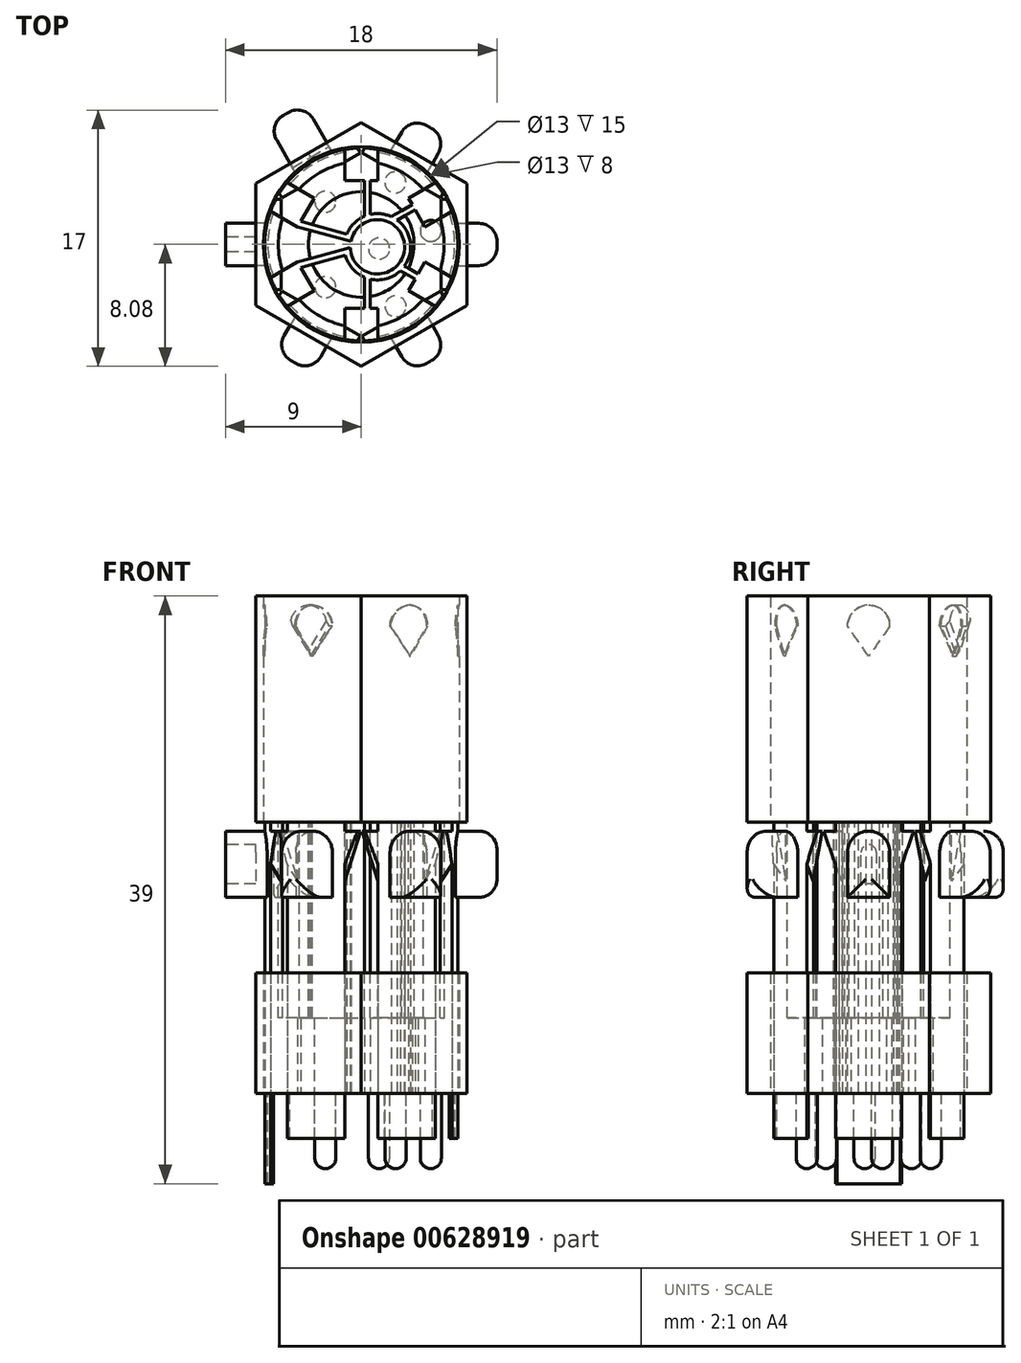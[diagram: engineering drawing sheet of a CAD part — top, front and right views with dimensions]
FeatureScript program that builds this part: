
annotation { "Feature Type Name" : "Feature", "Feature Type Description" : "" }
export const myFeature = defineFeature(function(context is Context, id is Id, definition is map)
    precondition{}
    {
        {
            var Q0;
            Q0=qCreatedBy(makeId("Top.planeOp"),FACE);
            var sketch = newSketch(context, id + "F0", { "sketchPlane" : qUnion([Q0])});
            skCircle(sketch, "E0.cCircle", {"center": v(0, 0) * mm, "radius": 7 * mm, "construction": true});
            skLineSegment(sketch, "E0.0", {"start": v(7, 4.04) * mm, "end": v(7, -4.04) * mm});
            skLineSegment(sketch, "E0.1", {"start": v(7, -4.04) * mm, "end": v(0, -8.08) * mm});
            skLineSegment(sketch, "E0.2", {"start": v(0, -8.08) * mm, "end": v(-7, -4.04) * mm});
            skLineSegment(sketch, "E0.3", {"start": v(-7, -4.04) * mm, "end": v(-7, 4.04) * mm});
            skLineSegment(sketch, "E0.4", {"start": v(-7, 4.04) * mm, "end": v(0, 8.08) * mm});
            skLineSegment(sketch, "E0.5", {"start": v(0, 8.08) * mm, "end": v(7, 4.04) * mm});
            skPoint(sketch, "E0.0.midPoint", {"position": v(7, 0) * mm});
            skCircle(sketch, "E1", {"center": v(0, 0) * mm, "radius": 6.4 * mm});
            skLineSegment(sketch, "E2", {"start": v(-1.1, 7.45) * mm, "end": v(1.1, 7.45) * mm});
            skLineSegment(sketch, "E3", {"start": v(1.1, 7.45) * mm, "end": v(1.1, 4.25) * mm});
            skLineSegment(sketch, "E4", {"start": v(1.1, -7.45) * mm, "end": v(-1.1, -7.45) * mm});
            skLineSegment(sketch, "E5", {"start": v(-1.1, -7.45) * mm, "end": v(-1.1, -4.25) * mm});
            skLineSegment(sketch, "E6", {"start": v(-7, 2.77) * mm, "end": v(-5.9, 4.68) * mm});
            skLineSegment(sketch, "E7", {"start": v(-5.9, 4.68) * mm, "end": v(-3.13, 3.08) * mm});
            skLineSegment(sketch, "E8", {"start": v(7, -2.77) * mm, "end": v(5.9, -4.68) * mm});
            skLineSegment(sketch, "E9", {"start": v(5.9, -4.68) * mm, "end": v(3.13, -3.08) * mm});
            skLineSegment(sketch, "E10", {"start": v(-7, -2.77) * mm, "end": v(-5.9, -4.68) * mm});
            skLineSegment(sketch, "E11", {"start": v(-5.9, -4.68) * mm, "end": v(-3.13, -3.08) * mm});
            skLineSegment(sketch, "E12", {"start": v(7, 2.77) * mm, "end": v(5.9, 4.68) * mm});
            skLineSegment(sketch, "E13", {"start": v(5.9, 4.68) * mm, "end": v(3.13, 3.08) * mm});
            skLineSegment(sketch, "E14", {"start": v(-1.1, 4.25) * mm, "end": v(1.1, 4.25) * mm});
            skLineSegment(sketch, "E15", {"start": v(-3.13, 3.08) * mm, "end": v(-4.23, 1.17) * mm});
            skLineSegment(sketch, "E16", {"start": v(-4.23, -1.17) * mm, "end": v(-3.13, -3.08) * mm});
            skLineSegment(sketch, "E17", {"start": v(-1.1, -4.25) * mm, "end": v(1.1, -4.25) * mm});
            skLineSegment(sketch, "E18", {"start": v(3.13, -3.08) * mm, "end": v(4.23, -1.17) * mm});
            skLineSegment(sketch, "E19", {"start": v(4.23, 1.17) * mm, "end": v(3.13, 3.08) * mm});
            skLineSegment(sketch, "E20.trimOffspring", {"start": v(4.23, 1.17) * mm, "end": v(7, 2.77) * mm});
            skLineSegment(sketch, "E21.trimOffspring", {"start": v(-4.23, -1.17) * mm, "end": v(-7, -2.77) * mm});
            skLineSegment(sketch, "E22.trimOffspring", {"start": v(-4.23, 1.17) * mm, "end": v(-7, 2.77) * mm});
            skLineSegment(sketch, "E23.trimOffspring", {"start": v(1.1, -4.25) * mm, "end": v(1.1, -7.45) * mm});
            skLineSegment(sketch, "E24.trimOffspring", {"start": v(4.23, -1.17) * mm, "end": v(7, -2.77) * mm});
            skLineSegment(sketch, "E25.trimOffspring", {"start": v(-1.1, 4.25) * mm, "end": v(-1.1, 7.45) * mm});
            skLineSegment(sketch, "E26", {"start": v(-4.02, 1.53) * mm, "end": v(-0.96, 0.68) * mm});
            skLineSegment(sketch, "E27", {"start": v(3.58, -2.3) * mm, "end": v(2.6, -1.75) * mm});
            skLineSegment(sketch, "E28", {"start": v(0.2, 4.25) * mm, "end": v(0.2, 1.86) * mm});
            skLineSegment(sketch, "E29", {"start": v(0.2, -4.25) * mm, "end": v(0.6, -4.25) * mm});
            skLineSegment(sketch, "E30", {"start": v(0.6, -4.25) * mm, "end": v(0.6, -2.3) * mm});
            skLineSegment(sketch, "E31", {"start": v(0.6, 4.25) * mm, "end": v(0.2, 4.25) * mm});
            skLineSegment(sketch, "E32", {"start": v(3.38, 2.64) * mm, "end": v(2, 1.84) * mm});
            skLineSegment(sketch, "E33", {"start": v(-4.23, -1.17) * mm, "end": v(-4.02, -1.53) * mm});
            skLineSegment(sketch, "E34", {"start": v(-4.02, -1.53) * mm, "end": v(-1.06, -0.7) * mm});
            skArc(sketch, "E35", {"start": v(2.86, -1.44) * mm, "mid": v(3.25, 0.18) * mm, "end": v(2.39, 1.6) * mm});
            skArc(sketch, "E36", {"start": v(2, 1.84) * mm, "mid": v(1.3, 2.03) * mm, "end": v(0.6, 2) * mm});
            skArc(sketch, "E37", {"start": v(0.6, -2.3) * mm, "mid": v(1.67, -2.28) * mm, "end": v(2.6, -1.75) * mm});
            skArc(sketch, "E38", {"start": v(-1.06, -0.7) * mm, "mid": v(-0.6, -1.59) * mm, "end": v(0.2, -2.18) * mm});
            skArc(sketch, "E39", {"start": v(0.2, 1.86) * mm, "mid": v(-0.5, 1.38) * mm, "end": v(-0.96, 0.68) * mm});
            skLineSegment(sketch, "E40.trimOffspring", {"start": v(0.2, -2.18) * mm, "end": v(0.2, -4.25) * mm});
            skLineSegment(sketch, "E41.trimOffspring", {"start": v(-0.7, 0.2) * mm, "end": v(-4.23, 1.17) * mm});
            skLineSegment(sketch, "E42.trimOffspring", {"start": v(2.86, -1.44) * mm, "end": v(3.78, -1.94) * mm});
            skLineSegment(sketch, "E43.trimOffspring", {"start": v(2.39, 1.6) * mm, "end": v(3.58, 2.3) * mm});
            skLineSegment(sketch, "E44.trimOffspring", {"start": v(-0.73, -0.2) * mm, "end": v(-4.23, -1.17) * mm});
            skLineSegment(sketch, "E45.trimOffspring", {"start": v(0.6, 2) * mm, "end": v(0.6, 4.25) * mm});
            skArc(sketch, "E46", {"start": v(-0.73, -0.2) * mm, "mid": v(2.87, -0.31) * mm, "end": v(-0.7, 0.2) * mm});
            skSolve(sketch);
        }
        {
            var Q0;
            {var subQ3=sQuery(id+"F0.wireOp",EDGE,"E1");var subQ5=sQuery(id+"F0.wireOp",EDGE,"E22.trimOffspring");var subQ12=makeQuery(id+"F0.imprint","INTERSECT",VERTEX,{"derivedFrom":[subQ3,subQ5]});Q0=makeQuery(id+"F0.imprint","IMPRINT",FACE,{"disambiguationData":[TD([[makeQuery(id+"F0.imprint","IMPRINT",EDGE,{"disambiguationData":[TD([[subQ12,-1.0]])],"derivedFrom":subQ3}),1.0]])]});}
            var Q1;
            {var subQ5=sQuery(id+"F0.wireOp",EDGE,"E25.trimOffspring");var subQ10=sQuery(id+"F0.wireOp",EDGE,"E1");var subQ12=makeQuery(id+"F0.imprint","INTERSECT",VERTEX,{"derivedFrom":[subQ10,subQ5]});Q1=makeQuery(id+"F0.imprint","IMPRINT",FACE,{"disambiguationData":[TD([[makeQuery(id+"F0.imprint","IMPRINT",EDGE,{"disambiguationData":[TD([[subQ12,-1.0]])],"derivedFrom":subQ10}),1.0]])]});}
            var Q2;
            {var subQ1=sQuery(id+"F0.wireOp",EDGE,"E13");var subQ3=sQuery(id+"F0.wireOp",EDGE,"E1");var subQ4=makeQuery(id+"F0.imprint","INTERSECT",VERTEX,{"derivedFrom":[subQ3,subQ1]});Q2=makeQuery(id+"F0.imprint","IMPRINT",FACE,{"disambiguationData":[TD([[makeQuery(id+"F0.imprint","IMPRINT",EDGE,{"disambiguationData":[TD([[subQ4,-1.0]])],"derivedFrom":subQ3}),1.0]])]});}
            var Q3;
            {var subQ0=sQuery(id+"F0.wireOp",EDGE,"E20.trimOffspring");var subQ3=sQuery(id+"F0.wireOp",EDGE,"E1");var subQ4=makeQuery(id+"F0.imprint","INTERSECT",VERTEX,{"derivedFrom":[subQ3,subQ0]});Q3=makeQuery(id+"F0.imprint","IMPRINT",FACE,{"disambiguationData":[TD([[makeQuery(id+"F0.imprint","IMPRINT",EDGE,{"disambiguationData":[TD([[subQ4,1.0]])],"derivedFrom":subQ3}),1.0]])]});}
            var Q4;
            {var subQ0=sQuery(id+"F0.wireOp",EDGE,"E23.trimOffspring");var subQ8=sQuery(id+"F0.wireOp",EDGE,"E1");var subQ12=makeQuery(id+"F0.imprint","INTERSECT",VERTEX,{"derivedFrom":[subQ8,subQ0]});Q4=makeQuery(id+"F0.imprint","IMPRINT",FACE,{"disambiguationData":[TD([[makeQuery(id+"F0.imprint","IMPRINT",EDGE,{"disambiguationData":[TD([[subQ12,-1.0]])],"derivedFrom":subQ8}),1.0]])]});}
            var Q5;
            {var subQ1=sQuery(id+"F0.wireOp",EDGE,"E11");var subQ5=sQuery(id+"F0.wireOp",EDGE,"E1");var subQ6=makeQuery(id+"F0.imprint","INTERSECT",VERTEX,{"derivedFrom":[subQ5,subQ1]});Q5=makeQuery(id+"F0.imprint","IMPRINT",FACE,{"disambiguationData":[TD([[makeQuery(id+"F0.imprint","IMPRINT",EDGE,{"disambiguationData":[TD([[subQ6,-1.0]])],"derivedFrom":subQ5}),1.0]])]});}
            extrude(context, id + "F1", {"entities" : qUnion([Q0, Q1, Q2, Q3, Q4, Q5]), "depth" : 33 * mm, "offsetDistance" : 25 * mm});
        }
        {
            var Q0;
            Q0=makeQuery(id+"F1.opExtrude","CAP_FACE",FACE,{"disambiguationData":[OSD([sQuery(id+"F0.wireOp",EDGE,"E1"),sQuery(id+"F0.wireOp",EDGE,"E7"),sQuery(id+"F0.wireOp",EDGE,"E14"),sQuery(id+"F0.wireOp",EDGE,"E15"),sQuery(id+"F0.wireOp",EDGE,"E25.trimOffspring"),sQuery(id+"F0.wireOp",EDGE,"E26"),sQuery(id+"F0.wireOp",EDGE,"E28")])],"isStart":false});
            cPlane(context, id + "F2", {"entities" : qUnion([Q0]), "cplaneType" : CPlaneType.OFFSET, "offset" : 0 * mm, "width" : 150 * mm, "height" : 150 * mm});
        }
        {
            var Q0;
            Q0=qCreatedBy(id+"F2.planeOp",FACE);
            var sketch = newSketch(context, id + "F3", { "sketchPlane" : qUnion([Q0])});
            skCircle(sketch, "E47", {"center": v(0, 0) * mm, "radius": 3.5 * mm});
            skCircle(sketch, "E48", {"center": v(0, 0) * mm, "radius": 5.5 * mm});
            skSolve(sketch);
        }
        {
            var Q0;
            Q0=makeQuery(id+"F3.imprint","IMPRINT",FACE,{"disambiguationData":[TD([[makeQuery(id+"F3.imprint","IMPRINT",EDGE,{"derivedFrom":sQuery(id+"F3.wireOp",EDGE,"E47")}),-1.0]])]});
            extrude(context, id + "F4", {"entities" : qUnion([Q0]), "operationType" : NewBodyOperationType.REMOVE, "oppositeDirection" : true, "depth" : 28 * mm, "offsetDistance" : 25 * mm});
        }
        {
            var Q0;
            Q0=makeQuery(id+"F1.opExtrude","CAP_FACE",FACE,{"disambiguationData":[OSD([sQuery(id+"F0.wireOp",EDGE,"E1"),sQuery(id+"F0.wireOp",EDGE,"E3"),sQuery(id+"F0.wireOp",EDGE,"E13"),sQuery(id+"F0.wireOp",EDGE,"E14"),sQuery(id+"F0.wireOp",EDGE,"E19"),sQuery(id+"F0.wireOp",EDGE,"E30"),sQuery(id+"F0.wireOp",EDGE,"E32")])],"isStart":true});
            var sketch = newSketch(context, id + "F5", { "sketchPlane" : qUnion([Q0])});
            skCircle(sketch, "E49", {"center": v(2.26, -4.12) * mm, "radius": 0.7 * mm});
            skLineSegment(sketch, "E50.0.0", {"start": v(3.38, -2.64) * mm, "end": v(2, -1.84) * mm, "construction": true});
            skLineSegment(sketch, "E50.0.3", {"start": v(1.1, -4.25) * mm, "end": v(1.1, -6.3) * mm, "construction": true});
            skArc(sketch, "E50.0.4", {"start": v(1.1, -6.3) * mm, "mid": v(3.2, -5.54) * mm, "end": v(4.91, -4.1) * mm, "construction": true});
            skLineSegment(sketch, "E50.0.5", {"start": v(4.91, -4.1) * mm, "end": v(3.13, -3.08) * mm, "construction": true});
            skLineSegment(sketch, "E50.0.6", {"start": v(3.13, -3.08) * mm, "end": v(3.38, -2.64) * mm, "construction": true});
            skLineSegment(sketch, "E51", {"start": v(0, 0) * mm, "end": v(3.56, -6.48) * mm, "construction": true});
            skSolve(sketch);
        }
        {
            var Q0;
            Q0=qSketchRegion(id+"F5",true);
            extrude(context, id + "F6", {"entities" : qUnion([Q0]), "operationType" : NewBodyOperationType.ADD, "depth" : 5 * mm, "offsetDistance" : 25 * mm});
        }
        {
            var Q0;
            Q0=makeQuery(id+"F6.opExtrude","CAP_FACE",FACE,{"disambiguationData":[OSD([sQuery(id+"F5.wireOp",EDGE,"E49")])],"isStart":false});
            fillet(context, id + "F7", {"entities" : qUnion([Q0]), "radius" : 0.7 * mm, "tangentPropagation" : true, "allowEdgeOverflow" : false});
        }
        {
            var Q0;
            Q0=makeQuery(id+"F1.opExtrude","CAP_FACE",FACE,{"disambiguationData":[OSD([sQuery(id+"F0.wireOp",EDGE,"E1"),sQuery(id+"F0.wireOp",EDGE,"E18"),sQuery(id+"F0.wireOp",EDGE,"E19"),sQuery(id+"F0.wireOp",EDGE,"E20.trimOffspring"),sQuery(id+"F0.wireOp",EDGE,"E24.trimOffspring"),sQuery(id+"F0.wireOp",EDGE,"E26"),sQuery(id+"F0.wireOp",EDGE,"E30"),sQuery(id+"F0.wireOp",EDGE,"E34")])],"isStart":true});
            var sketch = newSketch(context, id + "F8", { "sketchPlane" : qUnion([Q0])});
            skCircle(sketch, "E52", {"center": v(4.61, -0.9) * mm, "radius": 0.7 * mm});
            skLineSegment(sketch, "E53", {"start": v(0, 0) * mm, "end": v(6.9, -1.34) * mm, "construction": true});
            skSolve(sketch);
        }
        {
            var Q0;
            Q0=makeQuery(id+"F8.imprint","IMPRINT",FACE,{"disambiguationData":[TD([[makeQuery(id+"F8.imprint","IMPRINT",EDGE,{"derivedFrom":sQuery(id+"F8.wireOp",EDGE,"E52")}),1.0]])]});
            extrude(context, id + "F9", {"entities" : qUnion([Q0]), "operationType" : NewBodyOperationType.ADD, "depth" : 5 * mm, "offsetDistance" : 25 * mm});
        }
        {
            var Q0;
            Q0=makeQuery(id+"F9.opExtrude","CAP_FACE",FACE,{"disambiguationData":[OSD([sQuery(id+"F8.wireOp",EDGE,"E52")])],"isStart":false});
            fillet(context, id + "F10", {"entities" : qUnion([Q0]), "radius" : 0.7 * mm, "tangentPropagation" : true, "allowEdgeOverflow" : false});
        }
        {
            var Q0;
            Q0=makeQuery(id+"F1.opExtrude","CAP_FACE",FACE,{"disambiguationData":[OSD([sQuery(id+"F0.wireOp",EDGE,"E1"),sQuery(id+"F0.wireOp",EDGE,"E9"),sQuery(id+"F0.wireOp",EDGE,"E17"),sQuery(id+"F0.wireOp",EDGE,"E18"),sQuery(id+"F0.wireOp",EDGE,"E23.trimOffspring"),sQuery(id+"F0.wireOp",EDGE,"E27"),sQuery(id+"F0.wireOp",EDGE,"E30")])],"isStart":true});
            var sketch = newSketch(context, id + "F11", { "sketchPlane" : qUnion([Q0])});
            skCircle(sketch, "E54", {"center": v(2.28, 4.11) * mm, "radius": 0.7 * mm});
            skLineSegment(sketch, "E55", {"start": v(0, 0) * mm, "end": v(3.87, 6.99) * mm, "construction": true});
            skSolve(sketch);
        }
        {
            var Q0;
            Q0=qSketchRegion(id+"F11",true);
            extrude(context, id + "F12", {"entities" : qUnion([Q0]), "operationType" : NewBodyOperationType.ADD, "depth" : 5 * mm, "offsetDistance" : 25 * mm});
        }
        {
            var Q0;
            Q0=makeQuery(id+"F12.opExtrude","CAP_FACE",FACE,{"disambiguationData":[OSD([sQuery(id+"F11.wireOp",EDGE,"E54")])],"isStart":false});
            fillet(context, id + "F13", {"entities" : qUnion([Q0]), "radius" : 0.7 * mm, "tangentPropagation" : true, "allowEdgeOverflow" : false});
        }
        {
            var Q0;
            Q0=makeQuery(id+"F1.opExtrude","CAP_FACE",FACE,{"disambiguationData":[OSD([sQuery(id+"F0.wireOp",EDGE,"E1"),sQuery(id+"F0.wireOp",EDGE,"E5"),sQuery(id+"F0.wireOp",EDGE,"E11"),sQuery(id+"F0.wireOp",EDGE,"E16"),sQuery(id+"F0.wireOp",EDGE,"E17"),sQuery(id+"F0.wireOp",EDGE,"E27"),sQuery(id+"F0.wireOp",EDGE,"E28"),sQuery(id+"F0.wireOp",EDGE,"E34")])],"isStart":true});
            var sketch = newSketch(context, id + "F14", { "sketchPlane" : qUnion([Q0])});
            skLineSegment(sketch, "E56", {"start": v(0, 0) * mm, "end": v(-6.07, 7.24) * mm, "construction": true});
            skCircle(sketch, "E57", {"center": v(-2.38, 2.83) * mm, "radius": 0.7 * mm});
            skSolve(sketch);
        }
        {
            var Q0;
            Q0=makeQuery(id+"F14.imprint","IMPRINT",FACE,{"disambiguationData":[TD([[makeQuery(id+"F14.imprint","IMPRINT",EDGE,{"derivedFrom":sQuery(id+"F14.wireOp",EDGE,"E57")}),1.0]])]});
            extrude(context, id + "F15", {"entities" : qUnion([Q0]), "operationType" : NewBodyOperationType.ADD, "depth" : 5 * mm, "offsetDistance" : 25 * mm});
        }
        {
            var Q0;
            Q0=makeQuery(id+"F15.opExtrude","CAP_FACE",FACE,{"disambiguationData":[OSD([sQuery(id+"F14.wireOp",EDGE,"E57")])],"isStart":false});
            fillet(context, id + "F16", {"entities" : qUnion([Q0]), "radius" : 0.7 * mm, "tangentPropagation" : true, "allowEdgeOverflow" : false});
        }
        {
            var Q0;
            Q0=makeQuery(id+"F1.opExtrude","CAP_FACE",FACE,{"disambiguationData":[OSD([sQuery(id+"F0.wireOp",EDGE,"E1"),sQuery(id+"F0.wireOp",EDGE,"E7"),sQuery(id+"F0.wireOp",EDGE,"E14"),sQuery(id+"F0.wireOp",EDGE,"E15"),sQuery(id+"F0.wireOp",EDGE,"E25.trimOffspring"),sQuery(id+"F0.wireOp",EDGE,"E26"),sQuery(id+"F0.wireOp",EDGE,"E28"),sQuery(id+"F0.wireOp",EDGE,"E39")])],"isStart":true});
            var sketch = newSketch(context, id + "F17", { "sketchPlane" : qUnion([Q0])});
            skLineSegment(sketch, "E58", {"start": v(0, 0) * mm, "end": v(-5.7, -6.78) * mm, "construction": true});
            skCircle(sketch, "E59", {"center": v(-2.38, -2.83) * mm, "radius": 0.7 * mm});
            skSolve(sketch);
        }
        {
            var Q0;
            Q0=makeQuery(id+"F17.imprint","IMPRINT",FACE,{"disambiguationData":[TD([[makeQuery(id+"F17.imprint","IMPRINT",EDGE,{"derivedFrom":sQuery(id+"F17.wireOp",EDGE,"E59")}),1.0]])]});
            extrude(context, id + "F18", {"entities" : qUnion([Q0]), "operationType" : NewBodyOperationType.ADD, "depth" : 5 * mm, "offsetDistance" : 25 * mm});
        }
        {
            var Q0;
            Q0=makeQuery(id+"F18.opExtrude","CAP_FACE",FACE,{"disambiguationData":[OSD([sQuery(id+"F17.wireOp",EDGE,"E59")])],"isStart":false});
            fillet(context, id + "F19", {"entities" : qUnion([Q0]), "radius" : 0.7 * mm, "tangentPropagation" : true, "allowEdgeOverflow" : false});
        }
        {
            var Q0;
            Q0=makeQuery(id+"F1.opExtrude","CAP_FACE",FACE,{"disambiguationData":[OSD([sQuery(id+"F0.wireOp",EDGE,"E1"),sQuery(id+"F0.wireOp",EDGE,"E21.trimOffspring"),sQuery(id+"F0.wireOp",EDGE,"E22.trimOffspring"),sQuery(id+"F0.wireOp",EDGE,"E41.trimOffspring"),sQuery(id+"F0.wireOp",EDGE,"E44.trimOffspring"),sQuery(id+"F0.wireOp",EDGE,"E46")])],"isStart":true});
            var sketch = newSketch(context, id + "F20", { "sketchPlane" : qUnion([Q0])});
            skLineSegment(sketch, "E60", {"start": v(0, 0) * mm, "end": v(8.48, 1.96) * mm, "construction": true});
            skCircle(sketch, "E61", {"center": v(1.18, 0.27) * mm, "radius": 0.7 * mm});
            skSolve(sketch);
        }
        {
            var Q0;
            Q0=makeQuery(id+"F20.imprint","IMPRINT",FACE,{"disambiguationData":[TD([[makeQuery(id+"F20.imprint","IMPRINT",EDGE,{"derivedFrom":sQuery(id+"F20.wireOp",EDGE,"E61")}),1.0]])]});
            extrude(context, id + "F21", {"entities" : qUnion([Q0]), "operationType" : NewBodyOperationType.ADD, "depth" : 5 * mm, "offsetDistance" : 25 * mm});
        }
        {
            var Q0;
            Q0=makeQuery(id+"F21.opExtrude","CAP_FACE",FACE,{"disambiguationData":[OSD([sQuery(id+"F20.wireOp",EDGE,"E61")])],"isStart":false});
            fillet(context, id + "F22", {"entities" : qUnion([Q0]), "radius" : 0.7 * mm, "tangentPropagation" : true, "allowEdgeOverflow" : false});
        }
        {
            var Q0;
            {var subQ0=sQuery(id+"F0.wireOp",EDGE,"E41.trimOffspring");var subQ1=sQuery(id+"F0.wireOp",EDGE,"E46");var subQ2=sQuery(id+"F0.wireOp",EDGE,"E44.trimOffspring");Q0=makeQuery(id+"F4.boolean.opBoolean","SPLIT",FACE,{"disambiguationData":[TD([makeQuery(id+"F1.opExtrude","SWEPT_FACE",FACE,{"disambiguationData":[OSD([subQ0])]})])],"derivedFrom":makeQuery(id+"F1.opExtrude","CAP_FACE",FACE,{"disambiguationData":[OSD([sQuery(id+"F0.wireOp",EDGE,"E1"),sQuery(id+"F0.wireOp",EDGE,"E21.trimOffspring"),sQuery(id+"F0.wireOp",EDGE,"E22.trimOffspring"),subQ0,subQ2,subQ1])],"isStart":false})});}
            cPlane(context, id + "F23", {"entities" : qUnion([Q0]), "cplaneType" : CPlaneType.OFFSET, "offset" : 0 * mm, "width" : 150 * mm, "height" : 150 * mm});
        }
        {
            var Q0;
            Q0=qCreatedBy(id+"F23.planeOp",FACE);
            var sketch = newSketch(context, id + "F24", { "sketchPlane" : qUnion([Q0])});
            skCircle(sketch, "E62", {"center": v(0, 0) * mm, "radius": 7 * mm});
            skSolve(sketch);
        }
        {
            var Q0;
            Q0=makeQuery(id+"F24.imprint","IMPRINT",FACE,{"disambiguationData":[TD([[makeQuery(id+"F24.imprint","IMPRINT",EDGE,{"derivedFrom":sQuery(id+"F24.wireOp",EDGE,"E62")}),1.0]])]});
            extrude(context, id + "F25", {"entities" : qUnion([Q0]), "operationType" : NewBodyOperationType.REMOVE, "oppositeDirection" : true, "depth" : 15 * mm, "offsetDistance" : 25 * mm});
        }
        {
            var Q0;
            Q0=makeQuery(id+"F1.opExtrude","CAP_FACE",FACE,{"disambiguationData":[OSD([sQuery(id+"F0.wireOp",EDGE,"E1"),sQuery(id+"F0.wireOp",EDGE,"E18"),sQuery(id+"F0.wireOp",EDGE,"E19"),sQuery(id+"F0.wireOp",EDGE,"E20.trimOffspring"),sQuery(id+"F0.wireOp",EDGE,"E24.trimOffspring"),sQuery(id+"F0.wireOp",EDGE,"E35"),sQuery(id+"F0.wireOp",EDGE,"E42.trimOffspring"),sQuery(id+"F0.wireOp",EDGE,"E43.trimOffspring")])],"isStart":true});
            var sketch = newSketch(context, id + "F26", { "sketchPlane" : qUnion([Q0])});
            skArc(sketch, "E63.0", {"start": v(6.01, 2.2) * mm, "mid": v(6.4, 0) * mm, "end": v(6.01, -2.2) * mm});
            skArc(sketch, "E64.0", {"start": v(5.82, 2.13) * mm, "mid": v(6.2, 0) * mm, "end": v(5.82, -2.13) * mm});
            skLineSegment(sketch, "E65.0", {"start": v(4.88, -1.55) * mm, "end": v(6.01, -2.2) * mm});
            skLineSegment(sketch, "E66.0", {"start": v(4.23, 1.17) * mm, "end": v(6.01, 2.2) * mm});
            skSolve(sketch);
        }
        {
            var Q0;
            {var subQ0=sQuery(id+"F26.wireOp",EDGE,"E63.0");Q0=makeQuery(id+"F26.imprint","IMPRINT",FACE,{"disambiguationData":[TD([[makeQuery(id+"F26.imprint","IMPRINT",EDGE,{"derivedFrom":subQ0}),-1.0]])]});}
            extrude(context, id + "F27", {"entities" : qUnion([Q0]), "operationType" : NewBodyOperationType.ADD, "depth" : 3 * mm, "offsetDistance" : 25 * mm});
        }
        {
            var Q0;
            Q0=makeQuery(id+"F1.opExtrude","CAP_FACE",FACE,{"disambiguationData":[OSD([sQuery(id+"F0.wireOp",EDGE,"E1"),sQuery(id+"F0.wireOp",EDGE,"E9"),sQuery(id+"F0.wireOp",EDGE,"E17"),sQuery(id+"F0.wireOp",EDGE,"E18"),sQuery(id+"F0.wireOp",EDGE,"E23.trimOffspring"),sQuery(id+"F0.wireOp",EDGE,"E27"),sQuery(id+"F0.wireOp",EDGE,"E30"),sQuery(id+"F0.wireOp",EDGE,"E37")])],"isStart":true});
            var sketch = newSketch(context, id + "F28", { "sketchPlane" : qUnion([Q0])});
            skArc(sketch, "E67.0", {"start": v(1.1, 6.3) * mm, "mid": v(3.2, 5.54) * mm, "end": v(4.91, 4.1) * mm});
            skLineSegment(sketch, "E68.0", {"start": v(1.1, 4.25) * mm, "end": v(1.1, 6.3) * mm});
            skLineSegment(sketch, "E69.0", {"start": v(4.91, 4.1) * mm, "end": v(3.13, 3.08) * mm});
            skArc(sketch, "E70.0", {"start": v(1.07, 6.1) * mm, "mid": v(3.1, 5.37) * mm, "end": v(4.76, 3.98) * mm});
            skSolve(sketch);
        }
        {
            var Q0;
            Q0=qSketchRegion(id+"F28",true);
            extrude(context, id + "F29", {"entities" : qUnion([Q0]), "operationType" : NewBodyOperationType.ADD, "depth" : 3 * mm, "offsetDistance" : 25 * mm});
        }
        {
            var Q0;
            Q0=makeQuery(id+"F1.opExtrude","CAP_FACE",FACE,{"disambiguationData":[OSD([sQuery(id+"F0.wireOp",EDGE,"E1"),sQuery(id+"F0.wireOp",EDGE,"E5"),sQuery(id+"F0.wireOp",EDGE,"E11"),sQuery(id+"F0.wireOp",EDGE,"E16"),sQuery(id+"F0.wireOp",EDGE,"E17"),sQuery(id+"F0.wireOp",EDGE,"E34"),sQuery(id+"F0.wireOp",EDGE,"E38"),sQuery(id+"F0.wireOp",EDGE,"E40.trimOffspring")])],"isStart":true});
            var sketch = newSketch(context, id + "F30", { "sketchPlane" : qUnion([Q0])});
            skArc(sketch, "E71.0", {"start": v(-4.91, 4.1) * mm, "mid": v(-3.2, 5.54) * mm, "end": v(-1.1, 6.3) * mm});
            skLineSegment(sketch, "E72.0", {"start": v(-1.1, 6.3) * mm, "end": v(-1.1, 4.25) * mm});
            skLineSegment(sketch, "E73.0", {"start": v(-4.91, 4.1) * mm, "end": v(-3.13, 3.08) * mm});
            skArc(sketch, "E74.0", {"start": v(-4.76, 3.98) * mm, "mid": v(-3.1, 5.37) * mm, "end": v(-1.07, 6.1) * mm});
            skSolve(sketch);
        }
        {
            var Q0;
            Q0=qSketchRegion(id+"F30",true);
            extrude(context, id + "F31", {"entities" : qUnion([Q0]), "operationType" : NewBodyOperationType.ADD, "depth" : 3 * mm, "offsetDistance" : 25 * mm});
        }
        {
            var Q0;
            Q0=makeQuery(id+"F1.opExtrude","CAP_FACE",FACE,{"disambiguationData":[OSD([sQuery(id+"F0.wireOp",EDGE,"E1"),sQuery(id+"F0.wireOp",EDGE,"E21.trimOffspring"),sQuery(id+"F0.wireOp",EDGE,"E22.trimOffspring"),sQuery(id+"F0.wireOp",EDGE,"E41.trimOffspring"),sQuery(id+"F0.wireOp",EDGE,"E44.trimOffspring"),sQuery(id+"F0.wireOp",EDGE,"E46")])],"isStart":true});
            var sketch = newSketch(context, id + "F32", { "sketchPlane" : qUnion([Q0])});
            skLineSegment(sketch, "E75.0", {"start": v(-4.23, 1.17) * mm, "end": v(-6.01, 2.2) * mm});
            skArc(sketch, "E76.0", {"start": v(-6.01, -2.2) * mm, "mid": v(-6.4, 0) * mm, "end": v(-6.01, 2.2) * mm});
            skLineSegment(sketch, "E77.0", {"start": v(-4.23, -1.17) * mm, "end": v(-6.01, -2.2) * mm});
            skArc(sketch, "E78.0", {"start": v(-5.82, -2.13) * mm, "mid": v(-6.2, 0) * mm, "end": v(-5.82, 2.13) * mm});
            skSolve(sketch);
        }
        {
            var Q0;
            Q0=qSketchRegion(id+"F32",true);
            extrude(context, id + "F33", {"entities" : qUnion([Q0]), "operationType" : NewBodyOperationType.ADD, "depth" : 6 * mm, "offsetDistance" : 25 * mm});
        }
        {
            var Q0;
            Q0=makeQuery(id+"F1.opExtrude","CAP_FACE",FACE,{"disambiguationData":[OSD([sQuery(id+"F0.wireOp",EDGE,"E1"),sQuery(id+"F0.wireOp",EDGE,"E7"),sQuery(id+"F0.wireOp",EDGE,"E14"),sQuery(id+"F0.wireOp",EDGE,"E15"),sQuery(id+"F0.wireOp",EDGE,"E25.trimOffspring"),sQuery(id+"F0.wireOp",EDGE,"E26"),sQuery(id+"F0.wireOp",EDGE,"E28"),sQuery(id+"F0.wireOp",EDGE,"E39")])],"isStart":true});
            var sketch = newSketch(context, id + "F34", { "sketchPlane" : qUnion([Q0])});
            skArc(sketch, "E79.0", {"start": v(-1.1, -6.3) * mm, "mid": v(-3.2, -5.54) * mm, "end": v(-4.91, -4.1) * mm});
            skLineSegment(sketch, "E80.0", {"start": v(-1.1, -4.25) * mm, "end": v(-1.1, -6.3) * mm});
            skLineSegment(sketch, "E81.0", {"start": v(-4.91, -4.1) * mm, "end": v(-3.13, -3.08) * mm});
            skArc(sketch, "E82.0", {"start": v(-1.07, -6.1) * mm, "mid": v(-3.1, -5.37) * mm, "end": v(-4.76, -3.98) * mm});
            skSolve(sketch);
        }
        {
            var Q0;
            Q0=qSketchRegion(id+"F34",true);
            extrude(context, id + "F35", {"entities" : qUnion([Q0]), "operationType" : NewBodyOperationType.ADD, "depth" : 3 * mm, "offsetDistance" : 25 * mm});
        }
        {
            var Q0;
            Q0=makeQuery(id+"F1.opExtrude","CAP_FACE",FACE,{"disambiguationData":[OSD([sQuery(id+"F0.wireOp",EDGE,"E1"),sQuery(id+"F0.wireOp",EDGE,"E3"),sQuery(id+"F0.wireOp",EDGE,"E13"),sQuery(id+"F0.wireOp",EDGE,"E14"),sQuery(id+"F0.wireOp",EDGE,"E19"),sQuery(id+"F0.wireOp",EDGE,"E32"),sQuery(id+"F0.wireOp",EDGE,"E36"),sQuery(id+"F0.wireOp",EDGE,"E45.trimOffspring")])],"isStart":true});
            var sketch = newSketch(context, id + "F36", { "sketchPlane" : qUnion([Q0])});
            skArc(sketch, "E83.0", {"start": v(4.91, -4.1) * mm, "mid": v(3.2, -5.54) * mm, "end": v(1.1, -6.3) * mm});
            skLineSegment(sketch, "E84.0", {"start": v(1.1, -6.3) * mm, "end": v(1.1, -4.25) * mm});
            skLineSegment(sketch, "E85.0", {"start": v(4.91, -4.1) * mm, "end": v(3.13, -3.08) * mm});
            skArc(sketch, "E86.0", {"start": v(4.76, -3.98) * mm, "mid": v(3.1, -5.37) * mm, "end": v(1.07, -6.1) * mm});
            skSolve(sketch);
        }
        {
            var Q0;
            Q0=qSketchRegion(id+"F36",true);
            extrude(context, id + "F37", {"entities" : qUnion([Q0]), "operationType" : NewBodyOperationType.ADD, "depth" : 3 * mm, "offsetDistance" : 25 * mm});
        }
        {
            var Q0;
            Q0=qCreatedBy(makeId("Top.planeOp"),FACE);
            var sketch = newSketch(context, id + "F38", { "sketchPlane" : qUnion([Q0])});
            skCircle(sketch, "E87.cCircle", {"center": v(0, 0) * mm, "radius": 7 * mm, "construction": true});
            skLineSegment(sketch, "E87.0", {"start": v(7, 4.04) * mm, "end": v(7, -4.04) * mm});
            skLineSegment(sketch, "E87.1", {"start": v(7, -4.04) * mm, "end": v(0, -8.08) * mm});
            skLineSegment(sketch, "E87.2", {"start": v(0, -8.08) * mm, "end": v(-7, -4.04) * mm});
            skLineSegment(sketch, "E87.3", {"start": v(-7, -4.04) * mm, "end": v(-7, 4.04) * mm});
            skLineSegment(sketch, "E87.4", {"start": v(-7, 4.04) * mm, "end": v(0, 8.08) * mm});
            skLineSegment(sketch, "E87.5", {"start": v(0, 8.08) * mm, "end": v(7, 4.04) * mm});
            skPoint(sketch, "E87.0.midPoint", {"position": v(7, 0) * mm});
            skCircle(sketch, "E88", {"center": v(0, 0) * mm, "radius": 6.5 * mm});
            skSolve(sketch);
        }
        {
            var Q0;
            Q0=makeQuery(id+"F38.imprint","IMPRINT",FACE,{"disambiguationData":[TD([[makeQuery(id+"F38.imprint","IMPRINT",EDGE,{"derivedFrom":sQuery(id+"F38.wireOp",EDGE,"E87.0")}),-1.0]])]});
            extrude(context, id + "F39", {"entities" : qUnion([Q0]), "depth" : 33 * mm, "offsetDistance" : 25 * mm});
        }
        {
            var Q0;
            Q0=makeQuery(id+"F39.opExtrude","SWEPT_FACE",FACE,{"disambiguationData":[OSD([sQuery(id+"F38.wireOp",EDGE,"E87.5")])]});
            var sketch = newSketch(context, id + "F40", { "sketchPlane" : qUnion([Q0])});
            skLineSegment(sketch, "E89", {"start": v(-4.04, 16) * mm, "end": v(4.04, 16) * mm, "construction": true});
            skLineSegment(sketch, "E90", {"start": v(-4.04, 31) * mm, "end": v(4.04, 31) * mm, "construction": true});
            skLineSegment(sketch, "E91", {"start": v(0, 33.33) * mm, "end": v(0, 2) * mm, "construction": true});
            skLineSegment(sketch, "E92", {"start": v(0, 6.15) * mm, "end": v(-4.04, 6.15) * mm, "construction": true});
            skLineSegment(sketch, "E93", {"start": v(0, 6.15) * mm, "end": v(4.04, 6.15) * mm, "construction": true});
            skArc(sketch, "E94", {"start": v(1.4, 31) * mm, "mid": v(0, 32.4) * mm, "end": v(-1.4, 31) * mm});
            skLineSegment(sketch, "E95", {"start": v(-1.4, 31) * mm, "end": v(0, 29) * mm});
            skLineSegment(sketch, "E96", {"start": v(0, 29) * mm, "end": v(1.4, 31) * mm});
            skArc(sketch, "E97", {"start": v(1.4, 16) * mm, "mid": v(0, 17.4) * mm, "end": v(-1.4, 16) * mm});
            skLineSegment(sketch, "E98", {"start": v(1.4, 16) * mm, "end": v(1.4, 13) * mm});
            skLineSegment(sketch, "E99", {"start": v(1.4, 13) * mm, "end": v(-1.4, 13) * mm});
            skLineSegment(sketch, "E100", {"start": v(-1.4, 13) * mm, "end": v(-1.4, 16) * mm});
            skLineSegment(sketch, "E101", {"start": v(0, 17.4) * mm, "end": v(-3, 17.4) * mm});
            skLineSegment(sketch, "E102", {"start": v(-3, 17.4) * mm, "end": v(-1.4, 13) * mm});
            skLineSegment(sketch, "E103", {"start": v(0, 17.4) * mm, "end": v(3, 17.4) * mm});
            skLineSegment(sketch, "E104", {"start": v(3, 17.4) * mm, "end": v(1.4, 13) * mm});
            skLineSegment(sketch, "E105", {"start": v(1.4, 16) * mm, "end": v(1.4, 17.4) * mm});
            skLineSegment(sketch, "E106", {"start": v(-1.4, 16) * mm, "end": v(-1.4, 17.4) * mm});
            skSolve(sketch);
        }
        {
            var Q0;
            Q0=makeQuery(id+"F39.opExtrude","SWEPT_FACE",FACE,{"disambiguationData":[OSD([sQuery(id+"F38.wireOp",EDGE,"E87.3")])]});
            var sketch = newSketch(context, id + "F41", { "sketchPlane" : qUnion([Q0])});
            skLineSegment(sketch, "E107", {"start": v(-4.04, 16) * mm, "end": v(4.04, 16) * mm, "construction": true});
            skLineSegment(sketch, "E108", {"start": v(-4.04, 31) * mm, "end": v(4.04, 31) * mm, "construction": true});
            skLineSegment(sketch, "E109", {"start": v(0, 32.47) * mm, "end": v(0, 1.15) * mm, "construction": true});
            skLineSegment(sketch, "E110", {"start": v(0, 5.3) * mm, "end": v(-4.04, 5.3) * mm, "construction": true});
            skLineSegment(sketch, "E111", {"start": v(0, 5.3) * mm, "end": v(4.04, 5.3) * mm, "construction": true});
            skArc(sketch, "E112", {"start": v(1.4, 31) * mm, "mid": v(0, 32.4) * mm, "end": v(-1.4, 31) * mm});
            skLineSegment(sketch, "E113", {"start": v(-1.4, 31) * mm, "end": v(0, 29) * mm});
            skLineSegment(sketch, "E114", {"start": v(0, 29) * mm, "end": v(1.4, 31) * mm});
            skArc(sketch, "E115", {"start": v(1.4, 16) * mm, "mid": v(0, 17.4) * mm, "end": v(-1.4, 16) * mm});
            skLineSegment(sketch, "E116", {"start": v(1.4, 16) * mm, "end": v(1.4, 13) * mm});
            skLineSegment(sketch, "E117", {"start": v(1.4, 13) * mm, "end": v(-1.4, 13) * mm});
            skLineSegment(sketch, "E118", {"start": v(-1.4, 13) * mm, "end": v(-1.4, 16) * mm});
            skLineSegment(sketch, "E119", {"start": v(0, 17.4) * mm, "end": v(-3, 17.4) * mm});
            skLineSegment(sketch, "E120", {"start": v(0, 17.4) * mm, "end": v(3, 17.4) * mm});
            skLineSegment(sketch, "E121", {"start": v(3, 17.4) * mm, "end": v(1.4, 13) * mm});
            skLineSegment(sketch, "E122", {"start": v(-1.4, 13) * mm, "end": v(-3, 17.4) * mm});
            skLineSegment(sketch, "E123", {"start": v(-1.4, 16) * mm, "end": v(-1.4, 17.4) * mm});
            skLineSegment(sketch, "E124", {"start": v(1.4, 16) * mm, "end": v(1.4, 17.4) * mm});
            skSolve(sketch);
        }
        {
            var Q0;
            Q0=makeQuery(id+"F39.opExtrude","SWEPT_FACE",FACE,{"disambiguationData":[OSD([sQuery(id+"F38.wireOp",EDGE,"E87.4")])]});
            var sketch = newSketch(context, id + "F42", { "sketchPlane" : qUnion([Q0])});
            skLineSegment(sketch, "E125", {"start": v(-4.04, 16) * mm, "end": v(4.04, 16) * mm, "construction": true});
            skLineSegment(sketch, "E126", {"start": v(-4.04, 31) * mm, "end": v(4.04, 31) * mm, "construction": true});
            skLineSegment(sketch, "E127", {"start": v(0, 33.88) * mm, "end": v(0, 2.56) * mm, "construction": true});
            skLineSegment(sketch, "E128", {"start": v(0, 6.7) * mm, "end": v(-4.04, 6.7) * mm, "construction": true});
            skLineSegment(sketch, "E129", {"start": v(0, 6.7) * mm, "end": v(4.04, 6.7) * mm, "construction": true});
            skArc(sketch, "E130", {"start": v(1.4, 31) * mm, "mid": v(0, 32.4) * mm, "end": v(-1.4, 31) * mm});
            skLineSegment(sketch, "E131", {"start": v(-1.4, 31) * mm, "end": v(0, 29) * mm});
            skLineSegment(sketch, "E132", {"start": v(0, 29) * mm, "end": v(1.4, 31) * mm});
            skArc(sketch, "E133", {"start": v(1.4, 16) * mm, "mid": v(0, 17.4) * mm, "end": v(-1.4, 16) * mm});
            skLineSegment(sketch, "E134", {"start": v(1.4, 16) * mm, "end": v(1.4, 13) * mm});
            skLineSegment(sketch, "E135", {"start": v(1.4, 13) * mm, "end": v(-1.4, 13) * mm});
            skLineSegment(sketch, "E136", {"start": v(-1.4, 13) * mm, "end": v(-1.4, 16) * mm});
            skLineSegment(sketch, "E137", {"start": v(0, 17.4) * mm, "end": v(-3, 17.4) * mm});
            skLineSegment(sketch, "E138", {"start": v(-3, 17.4) * mm, "end": v(-1.4, 13) * mm});
            skLineSegment(sketch, "E139", {"start": v(-1.4, 16) * mm, "end": v(-1.4, 17.4) * mm});
            skLineSegment(sketch, "E140", {"start": v(0, 17.4) * mm, "end": v(3, 17.4) * mm});
            skLineSegment(sketch, "E141", {"start": v(3, 17.4) * mm, "end": v(1.4, 13) * mm});
            skLineSegment(sketch, "E142", {"start": v(1.4, 16) * mm, "end": v(1.4, 17.4) * mm});
            skSolve(sketch);
        }
        {
            var Q0;
            Q0=makeQuery(id+"F39.opExtrude","SWEPT_FACE",FACE,{"disambiguationData":[OSD([sQuery(id+"F38.wireOp",EDGE,"E87.2")])]});
            var sketch = newSketch(context, id + "F43", { "sketchPlane" : qUnion([Q0])});
            skLineSegment(sketch, "E143", {"start": v(-4.04, 16) * mm, "end": v(4.04, 16) * mm, "construction": true});
            skLineSegment(sketch, "E144", {"start": v(-4.04, 31) * mm, "end": v(4.04, 31) * mm, "construction": true});
            skLineSegment(sketch, "E145", {"start": v(0, 32.25) * mm, "end": v(0, 0.93) * mm, "construction": true});
            skLineSegment(sketch, "E146", {"start": v(0, 5.07) * mm, "end": v(-4.04, 5.07) * mm, "construction": true});
            skLineSegment(sketch, "E147", {"start": v(0, 5.07) * mm, "end": v(4.04, 5.07) * mm, "construction": true});
            skArc(sketch, "E148", {"start": v(1.4, 31) * mm, "mid": v(0, 32.4) * mm, "end": v(-1.4, 31) * mm});
            skLineSegment(sketch, "E149", {"start": v(-1.4, 31) * mm, "end": v(0, 29) * mm});
            skLineSegment(sketch, "E150", {"start": v(0, 29) * mm, "end": v(1.4, 31) * mm});
            skArc(sketch, "E151", {"start": v(1.4, 16) * mm, "mid": v(0, 17.4) * mm, "end": v(-1.4, 16) * mm});
            skLineSegment(sketch, "E152", {"start": v(1.4, 16) * mm, "end": v(1.4, 13) * mm});
            skLineSegment(sketch, "E153", {"start": v(1.4, 13) * mm, "end": v(-1.4, 13) * mm});
            skLineSegment(sketch, "E154", {"start": v(-1.4, 13) * mm, "end": v(-1.4, 16) * mm});
            skLineSegment(sketch, "E155", {"start": v(0, 17.4) * mm, "end": v(-3, 17.4) * mm});
            skPoint(sketch, "E155.endSnap0", {"position": v(0, 17.4) * mm});
            skLineSegment(sketch, "E156", {"start": v(-3, 17.4) * mm, "end": v(-1.4, 13) * mm});
            skLineSegment(sketch, "E157", {"start": v(0, 17.4) * mm, "end": v(3, 17.4) * mm});
            skLineSegment(sketch, "E158", {"start": v(3, 17.4) * mm, "end": v(1.4, 13) * mm});
            skLineSegment(sketch, "E159", {"start": v(1.4, 16) * mm, "end": v(1.4, 17.4) * mm});
            skLineSegment(sketch, "E160", {"start": v(-1.4, 16) * mm, "end": v(-1.4, 17.4) * mm});
            skSolve(sketch);
        }
        {
            var Q0;
            Q0=makeQuery(id+"F39.opExtrude","SWEPT_FACE",FACE,{"disambiguationData":[OSD([sQuery(id+"F38.wireOp",EDGE,"E87.1")])]});
            var sketch = newSketch(context, id + "F44", { "sketchPlane" : qUnion([Q0])});
            skLineSegment(sketch, "E161", {"start": v(-4.04, 16) * mm, "end": v(4.04, 16) * mm, "construction": true});
            skLineSegment(sketch, "E162", {"start": v(-4.04, 31) * mm, "end": v(4.04, 31) * mm, "construction": true});
            skLineSegment(sketch, "E163", {"start": v(0, 35.95) * mm, "end": v(0, 4.63) * mm, "construction": true});
            skLineSegment(sketch, "E164", {"start": v(0, 8.76) * mm, "end": v(-4.04, 8.76) * mm, "construction": true});
            skLineSegment(sketch, "E165", {"start": v(0, 8.76) * mm, "end": v(4.04, 8.76) * mm, "construction": true});
            skArc(sketch, "E166", {"start": v(1.4, 31) * mm, "mid": v(0, 32.4) * mm, "end": v(-1.4, 31) * mm});
            skLineSegment(sketch, "E167", {"start": v(-1.4, 31) * mm, "end": v(0, 29) * mm});
            skLineSegment(sketch, "E168", {"start": v(0, 29) * mm, "end": v(1.4, 31) * mm});
            skArc(sketch, "E169", {"start": v(1.4, 16) * mm, "mid": v(0, 17.4) * mm, "end": v(-1.4, 16) * mm});
            skLineSegment(sketch, "E170", {"start": v(1.4, 16) * mm, "end": v(1.4, 13) * mm});
            skLineSegment(sketch, "E171", {"start": v(1.4, 13) * mm, "end": v(-1.4, 13) * mm});
            skLineSegment(sketch, "E172", {"start": v(-1.4, 13) * mm, "end": v(-1.4, 16) * mm});
            skLineSegment(sketch, "E173", {"start": v(0, 17.4) * mm, "end": v(-3, 17.4) * mm});
            skLineSegment(sketch, "E174", {"start": v(-3, 17.4) * mm, "end": v(-1.4, 13) * mm});
            skLineSegment(sketch, "E175", {"start": v(0, 17.4) * mm, "end": v(3, 17.4) * mm});
            skLineSegment(sketch, "E176", {"start": v(3, 17.4) * mm, "end": v(1.4, 13) * mm});
            skLineSegment(sketch, "E177", {"start": v(1.4, 16) * mm, "end": v(1.4, 17.4) * mm});
            skLineSegment(sketch, "E178", {"start": v(-1.4, 16) * mm, "end": v(-1.5, 17.4) * mm});
            skSolve(sketch);
        }
        {
            var Q0;
            Q0=makeQuery(id+"F39.opExtrude","SWEPT_FACE",FACE,{"disambiguationData":[OSD([sQuery(id+"F38.wireOp",EDGE,"E87.0")])]});
            var sketch = newSketch(context, id + "F45", { "sketchPlane" : qUnion([Q0])});
            skLineSegment(sketch, "E179", {"start": v(-4.04, 16) * mm, "end": v(4.04, 16) * mm, "construction": true});
            skLineSegment(sketch, "E180", {"start": v(-4.04, 31) * mm, "end": v(4.04, 31) * mm, "construction": true});
            skLineSegment(sketch, "E181", {"start": v(0, 33.37) * mm, "end": v(0, 2.05) * mm, "construction": true});
            skLineSegment(sketch, "E182", {"start": v(0, 6.2) * mm, "end": v(-4.04, 6.2) * mm, "construction": true});
            skLineSegment(sketch, "E183", {"start": v(0, 6.2) * mm, "end": v(4.04, 6.2) * mm, "construction": true});
            skArc(sketch, "E184", {"start": v(1.4, 31) * mm, "mid": v(0, 32.4) * mm, "end": v(-1.4, 31) * mm});
            skLineSegment(sketch, "E185", {"start": v(-1.4, 31) * mm, "end": v(0, 29) * mm});
            skLineSegment(sketch, "E186", {"start": v(0, 29) * mm, "end": v(1.4, 31) * mm});
            skArc(sketch, "E187", {"start": v(1.4, 16) * mm, "mid": v(0, 17.4) * mm, "end": v(-1.4, 16) * mm});
            skLineSegment(sketch, "E188", {"start": v(1.4, 16) * mm, "end": v(1.4, 13) * mm});
            skLineSegment(sketch, "E189", {"start": v(1.4, 13) * mm, "end": v(-1.4, 13) * mm});
            skLineSegment(sketch, "E190", {"start": v(-1.4, 13) * mm, "end": v(-1.4, 16) * mm});
            skLineSegment(sketch, "E191", {"start": v(0, 17.4) * mm, "end": v(-3, 17.4) * mm});
            skLineSegment(sketch, "E192", {"start": v(-3, 17.4) * mm, "end": v(-1.4, 13) * mm});
            skLineSegment(sketch, "E193", {"start": v(0, 17.4) * mm, "end": v(3, 17.4) * mm});
            skLineSegment(sketch, "E194", {"start": v(3, 17.4) * mm, "end": v(1.4, 13) * mm});
            skLineSegment(sketch, "E195", {"start": v(1.4, 16) * mm, "end": v(1.4, 17.4) * mm});
            skLineSegment(sketch, "E196", {"start": v(-1.4, 16) * mm, "end": v(-1.4, 17.4) * mm});
            skSolve(sketch);
        }
        {
            var Q0;
            Q0=makeQuery(id+"F40.imprint","IMPRINT",FACE,{"disambiguationData":[TD([[makeQuery(id+"F40.imprint","IMPRINT",EDGE,{"derivedFrom":sQuery(id+"F40.wireOp",EDGE,"E100")}),1.0]])]});
            var Q1;
            Q1=makeQuery(id+"F40.imprint","IMPRINT",FACE,{"disambiguationData":[TD([[makeQuery(id+"F40.imprint","IMPRINT",EDGE,{"derivedFrom":sQuery(id+"F40.wireOp",EDGE,"E98")}),1.0]])]});
            extrude(context, id + "F46", {"entities" : qUnion([Q0, Q1]), "operationType" : NewBodyOperationType.ADD, "oppositeDirection" : true, "depth" : 1.7 * mm, "offsetDistance" : 25 * mm});
        }
        {
            var Q0;
            {var subQ3=sQuery(id+"F41.wireOp",EDGE,"E119");Q0=makeQuery(id+"F41.imprint","IMPRINT",FACE,{"disambiguationData":[TD([[makeQuery(id+"F41.imprint","IMPRINT",EDGE,{"derivedFrom":subQ3}),1.0]])]});}
            var Q1;
            {var subQ0=sQuery(id+"F41.wireOp",EDGE,"E118");Q1=makeQuery(id+"F41.imprint","IMPRINT",FACE,{"disambiguationData":[TD([[makeQuery(id+"F41.imprint","IMPRINT",EDGE,{"derivedFrom":subQ0}),1.0]])]});}
            var Q2;
            {var subQ0=sQuery(id+"F41.wireOp",EDGE,"E116");Q2=makeQuery(id+"F41.imprint","IMPRINT",FACE,{"disambiguationData":[TD([[makeQuery(id+"F41.imprint","IMPRINT",EDGE,{"derivedFrom":subQ0}),1.0]])]});}
            extrude(context, id + "F47", {"entities" : qUnion([Q0, Q1, Q2]), "operationType" : NewBodyOperationType.ADD, "oppositeDirection" : true, "depth" : 1.7 * mm, "offsetDistance" : 25 * mm});
        }
        {
            var Q0;
            Q0=makeQuery(id+"F42.imprint","IMPRINT",FACE,{"disambiguationData":[TD([[makeQuery(id+"F42.imprint","IMPRINT",EDGE,{"derivedFrom":sQuery(id+"F42.wireOp",EDGE,"E136")}),1.0]])]});
            var Q1;
            Q1=makeQuery(id+"F42.imprint","IMPRINT",FACE,{"disambiguationData":[TD([[makeQuery(id+"F42.imprint","IMPRINT",EDGE,{"derivedFrom":sQuery(id+"F42.wireOp",EDGE,"E134")}),1.0]])]});
            extrude(context, id + "F48", {"entities" : qUnion([Q0, Q1]), "operationType" : NewBodyOperationType.ADD, "oppositeDirection" : true, "depth" : 1.7 * mm, "offsetDistance" : 25 * mm});
        }
        {
            var Q0;
            Q0=makeQuery(id+"F43.imprint","IMPRINT",FACE,{"disambiguationData":[TD([[makeQuery(id+"F43.imprint","IMPRINT",EDGE,{"derivedFrom":sQuery(id+"F43.wireOp",EDGE,"E154")}),1.0]])]});
            var Q1;
            Q1=makeQuery(id+"F43.imprint","IMPRINT",FACE,{"disambiguationData":[TD([[makeQuery(id+"F43.imprint","IMPRINT",EDGE,{"derivedFrom":sQuery(id+"F43.wireOp",EDGE,"E152")}),1.0]])]});
            extrude(context, id + "F49", {"entities" : qUnion([Q0, Q1]), "operationType" : NewBodyOperationType.ADD, "oppositeDirection" : true, "depth" : 1.7 * mm, "offsetDistance" : 25 * mm});
        }
        {
            var Q0;
            Q0=makeQuery(id+"F44.imprint","IMPRINT",FACE,{"disambiguationData":[TD([[makeQuery(id+"F44.imprint","IMPRINT",EDGE,{"derivedFrom":sQuery(id+"F44.wireOp",EDGE,"E172")}),1.0]])]});
            var Q1;
            Q1=makeQuery(id+"F44.imprint","IMPRINT",FACE,{"disambiguationData":[TD([[makeQuery(id+"F44.imprint","IMPRINT",EDGE,{"derivedFrom":sQuery(id+"F44.wireOp",EDGE,"E170")}),1.0]])]});
            extrude(context, id + "F50", {"entities" : qUnion([Q0, Q1]), "operationType" : NewBodyOperationType.ADD, "oppositeDirection" : true, "depth" : 1.7 * mm, "offsetDistance" : 25 * mm});
        }
        {
            var Q0;
            Q0=makeQuery(id+"F45.imprint","IMPRINT",FACE,{"disambiguationData":[TD([[makeQuery(id+"F45.imprint","IMPRINT",EDGE,{"derivedFrom":sQuery(id+"F45.wireOp",EDGE,"E190")}),1.0]])]});
            var Q1;
            Q1=makeQuery(id+"F45.imprint","IMPRINT",FACE,{"disambiguationData":[TD([[makeQuery(id+"F45.imprint","IMPRINT",EDGE,{"derivedFrom":sQuery(id+"F45.wireOp",EDGE,"E188")}),1.0]])]});
            extrude(context, id + "F51", {"entities" : qUnion([Q0, Q1]), "operationType" : NewBodyOperationType.ADD, "oppositeDirection" : true, "depth" : 1.7 * mm, "offsetDistance" : 25 * mm});
        }
        {
            var Q0;
            {var subQ2=sQuery(id+"F0.wireOp",EDGE,"E5");var subQ3=makeQuery(id+"F1.opExtrude","SWEPT_FACE",FACE,{"disambiguationData":[OSD([subQ2])]});Q0=makeQuery(id+"F25.boolean.opBoolean","COPY",FACE,{"disambiguationData":[TD([subQ3])],"derivedFrom":makeQuery(id+"F25.opExtrude","CAP_FACE",FACE,{"disambiguationData":[OSD([sQuery(id+"F24.wireOp",EDGE,"E62")])],"isStart":false})});}
            var sketch = newSketch(context, id + "F52", { "sketchPlane" : qUnion([Q0])});
            skCircle(sketch, "E197", {"center": v(0, 0) * mm, "radius": 5.5 * mm});
            skCircle(sketch, "E198", {"center": v(0, 0) * mm, "radius": 6.4 * mm});
            skCircle(sketch, "E199", {"center": v(0, 0) * mm, "radius": 8.5 * mm});
            skCircle(sketch, "E200", {"center": v(0, 0) * mm, "radius": 3.5 * mm});
            skSolve(sketch);
        }
        {
            var Q0;
            Q0=makeQuery(id+"F52.imprint","IMPRINT",FACE,{"disambiguationData":[TD([[makeQuery(id+"F52.imprint","IMPRINT",EDGE,{"derivedFrom":sQuery(id+"F52.wireOp",EDGE,"E199")}),1.0]])]});
            var Q1;
            {var subQ0=sQuery(id+"F52.wireOp",EDGE,"E197");Q1=makeQuery(id+"F52.imprint","IMPRINT",FACE,{"disambiguationData":[TD([[makeQuery(id+"F52.imprint","IMPRINT",EDGE,{"disambiguationData":[OD(0.0)],"derivedFrom":subQ0}),1.0]])]});}
            extrude(context, id + "F53", {"entities" : qUnion([Q0, Q1]), "operationType" : NewBodyOperationType.REMOVE, "oppositeDirection" : true, "depth" : 10 * mm, "offsetDistance" : 25 * mm});
        }
        {
            var Q0;
            Q0=makeQuery(id+"F40.imprint","IMPRINT",FACE,{"disambiguationData":[TD([[makeQuery(id+"F40.imprint","IMPRINT",EDGE,{"derivedFrom":sQuery(id+"F40.wireOp",EDGE,"E94")}),1.0]])]});
            var Q1;
            {var subQ0=sQuery(id+"F0.wireOp",EDGE,"E1");Q1=makeQuery(id+"F1.opExtrude","SWEPT_FACE",FACE,{"disambiguationData":[OSD([subQ0]),TDD([makeQuery(id+"F0.imprint","IMPRINT",EDGE,{"disambiguationData":[TD([[makeQuery(id+"F0.imprint","INTERSECT",VERTEX,{"derivedFrom":[subQ0,sQuery(id+"F0.wireOp",EDGE,"E13")]}),-1.0]])],"derivedFrom":subQ0})])]});}
            extrude(context, id + "F54", {"entities" : qUnion([Q0]), "operationType" : NewBodyOperationType.ADD, "endBound" : BoundingType.UP_TO_SURFACE, "oppositeDirection" : true, "depth" : 25 * mm, "endBoundEntityFace" : qUnion([Q1]), "offsetDistance" : 25 * mm});
        }
        {
            var Q0;
            Q0=makeQuery(id+"F40.imprint","IMPRINT",FACE,{"disambiguationData":[TD([[makeQuery(id+"F40.imprint","IMPRINT",EDGE,{"derivedFrom":sQuery(id+"F40.wireOp",EDGE,"E97")}),1.0]])]});
            var Q1;
            {var subQ0=sQuery(id+"F0.wireOp",EDGE,"E1");Q1=makeQuery(id+"F1.opExtrude","SWEPT_FACE",FACE,{"disambiguationData":[OSD([subQ0]),TDD([makeQuery(id+"F0.imprint","IMPRINT",EDGE,{"disambiguationData":[TD([[makeQuery(id+"F0.imprint","INTERSECT",VERTEX,{"derivedFrom":[subQ0,sQuery(id+"F0.wireOp",EDGE,"E13")]}),-1.0]])],"derivedFrom":subQ0})])]});}
            extrude(context, id + "F55", {"entities" : qUnion([Q0]), "operationType" : NewBodyOperationType.ADD, "endBound" : BoundingType.UP_TO_SURFACE, "oppositeDirection" : true, "depth" : 25 * mm, "endBoundEntityFace" : qUnion([Q1]), "offsetDistance" : 25 * mm, "hasSecondDirection" : true, "secondDirectionOppositeDirection" : false, "secondDirectionDepth" : 2 * mm});
        }
        {
            var Q0;
            Q0=makeQuery(id+"F41.imprint","IMPRINT",FACE,{"disambiguationData":[TD([[makeQuery(id+"F41.imprint","IMPRINT",EDGE,{"derivedFrom":sQuery(id+"F41.wireOp",EDGE,"E112")}),1.0]])]});
            var Q1;
            {var subQ0=sQuery(id+"F0.wireOp",EDGE,"E1");Q1=makeQuery(id+"F1.opExtrude","SWEPT_FACE",FACE,{"disambiguationData":[OSD([subQ0]),TDD([makeQuery(id+"F0.imprint","IMPRINT",EDGE,{"disambiguationData":[TD([[makeQuery(id+"F0.imprint","INTERSECT",VERTEX,{"derivedFrom":[subQ0,sQuery(id+"F0.wireOp",EDGE,"E22.trimOffspring")]}),-1.0]])],"derivedFrom":subQ0})])]});}
            extrude(context, id + "F56", {"entities" : qUnion([Q0]), "operationType" : NewBodyOperationType.ADD, "endBound" : BoundingType.UP_TO_SURFACE, "oppositeDirection" : true, "depth" : 25 * mm, "endBoundEntityFace" : qUnion([Q1]), "offsetDistance" : 25 * mm});
        }
        {
            var Q0;
            Q0=makeQuery(id+"F41.imprint","IMPRINT",FACE,{"disambiguationData":[TD([[makeQuery(id+"F41.imprint","IMPRINT",EDGE,{"derivedFrom":sQuery(id+"F41.wireOp",EDGE,"E115")}),1.0]])]});
            var Q1;
            {var subQ0=sQuery(id+"F0.wireOp",EDGE,"E1");Q1=makeQuery(id+"F1.opExtrude","SWEPT_FACE",FACE,{"disambiguationData":[OSD([subQ0]),TDD([makeQuery(id+"F0.imprint","IMPRINT",EDGE,{"disambiguationData":[TD([[makeQuery(id+"F0.imprint","INTERSECT",VERTEX,{"derivedFrom":[subQ0,sQuery(id+"F0.wireOp",EDGE,"E22.trimOffspring")]}),-1.0]])],"derivedFrom":subQ0})])]});}
            extrude(context, id + "F57", {"entities" : qUnion([Q0]), "operationType" : NewBodyOperationType.ADD, "endBound" : BoundingType.UP_TO_SURFACE, "oppositeDirection" : true, "depth" : 25 * mm, "endBoundEntityFace" : qUnion([Q1]), "offsetDistance" : 25 * mm, "hasSecondDirection" : true, "secondDirectionOppositeDirection" : false, "secondDirectionDepth" : 2 * mm});
        }
        {
            var Q0;
            Q0=makeQuery(id+"F42.imprint","IMPRINT",FACE,{"disambiguationData":[TD([[makeQuery(id+"F42.imprint","IMPRINT",EDGE,{"derivedFrom":sQuery(id+"F42.wireOp",EDGE,"E130")}),1.0]])]});
            var Q1;
            {var subQ0=sQuery(id+"F0.wireOp",EDGE,"E1");Q1=makeQuery(id+"F35.boolean.opBoolean","MERGE",FACE,{"derivedFrom":[makeQuery(id+"F1.opExtrude","SWEPT_FACE",FACE,{"disambiguationData":[OSD([subQ0]),TDD([makeQuery(id+"F0.imprint","IMPRINT",EDGE,{"disambiguationData":[TD([[makeQuery(id+"F0.imprint","INTERSECT",VERTEX,{"derivedFrom":[subQ0,sQuery(id+"F0.wireOp",EDGE,"E25.trimOffspring")]}),-1.0]])],"derivedFrom":subQ0})])]}),makeQuery(id+"F35.opExtrude","SWEPT_FACE",FACE,{"disambiguationData":[OSD([sQuery(id+"F34.wireOp",EDGE,"E79.0")])]})]});}
            extrude(context, id + "F58", {"entities" : qUnion([Q0]), "endBound" : BoundingType.UP_TO_SURFACE, "oppositeDirection" : true, "depth" : 25 * mm, "endBoundEntityFace" : qUnion([Q1]), "offsetDistance" : 25 * mm});
        }
        {
            var Q0;
            Q0=makeQuery(id+"F42.imprint","IMPRINT",FACE,{"disambiguationData":[TD([[makeQuery(id+"F42.imprint","IMPRINT",EDGE,{"derivedFrom":sQuery(id+"F42.wireOp",EDGE,"E133")}),1.0]])]});
            var Q1;
            {var subQ0=sQuery(id+"F0.wireOp",EDGE,"E1");Q1=makeQuery(id+"F35.boolean.opBoolean","MERGE",FACE,{"derivedFrom":[makeQuery(id+"F1.opExtrude","SWEPT_FACE",FACE,{"disambiguationData":[OSD([subQ0]),TDD([makeQuery(id+"F0.imprint","IMPRINT",EDGE,{"disambiguationData":[TD([[makeQuery(id+"F0.imprint","INTERSECT",VERTEX,{"derivedFrom":[subQ0,sQuery(id+"F0.wireOp",EDGE,"E25.trimOffspring")]}),-1.0]])],"derivedFrom":subQ0})])]}),makeQuery(id+"F35.opExtrude","SWEPT_FACE",FACE,{"disambiguationData":[OSD([sQuery(id+"F34.wireOp",EDGE,"E79.0")])]})]});}
            extrude(context, id + "F59", {"entities" : qUnion([Q0]), "operationType" : NewBodyOperationType.ADD, "endBound" : BoundingType.UP_TO_SURFACE, "oppositeDirection" : true, "depth" : 25 * mm, "endBoundEntityFace" : qUnion([Q1]), "offsetDistance" : 25 * mm, "hasSecondDirection" : true, "secondDirectionOppositeDirection" : false, "secondDirectionDepth" : 3 * mm});
        }
        {
            var Q0;
            Q0=makeQuery(id+"F43.imprint","IMPRINT",FACE,{"disambiguationData":[TD([[makeQuery(id+"F43.imprint","IMPRINT",EDGE,{"derivedFrom":sQuery(id+"F43.wireOp",EDGE,"E148")}),1.0]])]});
            var Q1;
            {var subQ0=sQuery(id+"F0.wireOp",EDGE,"E1");Q1=makeQuery(id+"F31.boolean.opBoolean","MERGE",FACE,{"derivedFrom":[makeQuery(id+"F1.opExtrude","SWEPT_FACE",FACE,{"disambiguationData":[OSD([subQ0]),TDD([makeQuery(id+"F0.imprint","IMPRINT",EDGE,{"disambiguationData":[TD([[makeQuery(id+"F0.imprint","INTERSECT",VERTEX,{"derivedFrom":[subQ0,sQuery(id+"F0.wireOp",EDGE,"E11")]}),-1.0]])],"derivedFrom":subQ0})])]}),makeQuery(id+"F31.opExtrude","SWEPT_FACE",FACE,{"disambiguationData":[OSD([sQuery(id+"F30.wireOp",EDGE,"E71.0")])]})]});}
            extrude(context, id + "F60", {"entities" : qUnion([Q0]), "operationType" : NewBodyOperationType.ADD, "endBound" : BoundingType.UP_TO_SURFACE, "oppositeDirection" : true, "depth" : 25 * mm, "endBoundEntityFace" : qUnion([Q1]), "offsetDistance" : 25 * mm});
        }
        {
            var Q0;
            Q0=makeQuery(id+"F43.imprint","IMPRINT",FACE,{"disambiguationData":[TD([[makeQuery(id+"F43.imprint","IMPRINT",EDGE,{"derivedFrom":sQuery(id+"F43.wireOp",EDGE,"E151")}),1.0]])]});
            var Q1;
            {var subQ0=sQuery(id+"F0.wireOp",EDGE,"E1");Q1=makeQuery(id+"F31.boolean.opBoolean","MERGE",FACE,{"derivedFrom":[makeQuery(id+"F1.opExtrude","SWEPT_FACE",FACE,{"disambiguationData":[OSD([subQ0]),TDD([makeQuery(id+"F0.imprint","IMPRINT",EDGE,{"disambiguationData":[TD([[makeQuery(id+"F0.imprint","INTERSECT",VERTEX,{"derivedFrom":[subQ0,sQuery(id+"F0.wireOp",EDGE,"E11")]}),-1.0]])],"derivedFrom":subQ0})])]}),makeQuery(id+"F31.opExtrude","SWEPT_FACE",FACE,{"disambiguationData":[OSD([sQuery(id+"F30.wireOp",EDGE,"E71.0")])]})]});}
            extrude(context, id + "F61", {"entities" : qUnion([Q0]), "operationType" : NewBodyOperationType.ADD, "endBound" : BoundingType.UP_TO_SURFACE, "oppositeDirection" : true, "depth" : 25 * mm, "endBoundEntityFace" : qUnion([Q1]), "offsetDistance" : 25 * mm, "hasSecondDirection" : true, "secondDirectionOppositeDirection" : false, "secondDirectionDepth" : 2 * mm});
        }
        {
            var Q0;
            Q0=makeQuery(id+"F44.imprint","IMPRINT",FACE,{"disambiguationData":[TD([[makeQuery(id+"F44.imprint","IMPRINT",EDGE,{"derivedFrom":sQuery(id+"F44.wireOp",EDGE,"E166")}),1.0]])]});
            var Q1;
            {var subQ0=sQuery(id+"F0.wireOp",EDGE,"E1");Q1=makeQuery(id+"F29.boolean.opBoolean","MERGE",FACE,{"derivedFrom":[makeQuery(id+"F1.opExtrude","SWEPT_FACE",FACE,{"disambiguationData":[OSD([subQ0]),TDD([makeQuery(id+"F0.imprint","IMPRINT",EDGE,{"disambiguationData":[TD([[makeQuery(id+"F0.imprint","INTERSECT",VERTEX,{"derivedFrom":[subQ0,sQuery(id+"F0.wireOp",EDGE,"E23.trimOffspring")]}),-1.0]])],"derivedFrom":subQ0})])]}),makeQuery(id+"F29.opExtrude","SWEPT_FACE",FACE,{"disambiguationData":[OSD([sQuery(id+"F28.wireOp",EDGE,"E67.0")])]})]});}
            extrude(context, id + "F62", {"entities" : qUnion([Q0]), "operationType" : NewBodyOperationType.ADD, "endBound" : BoundingType.UP_TO_SURFACE, "oppositeDirection" : true, "depth" : 25 * mm, "endBoundEntityFace" : qUnion([Q1]), "offsetDistance" : 25 * mm});
        }
        {
            var Q0;
            Q0=makeQuery(id+"F44.imprint","IMPRINT",FACE,{"disambiguationData":[TD([[makeQuery(id+"F44.imprint","IMPRINT",EDGE,{"derivedFrom":sQuery(id+"F44.wireOp",EDGE,"E169")}),1.0]])]});
            var Q1;
            {var subQ0=sQuery(id+"F0.wireOp",EDGE,"E1");Q1=makeQuery(id+"F29.boolean.opBoolean","MERGE",FACE,{"derivedFrom":[makeQuery(id+"F1.opExtrude","SWEPT_FACE",FACE,{"disambiguationData":[OSD([subQ0]),TDD([makeQuery(id+"F0.imprint","IMPRINT",EDGE,{"disambiguationData":[TD([[makeQuery(id+"F0.imprint","INTERSECT",VERTEX,{"derivedFrom":[subQ0,sQuery(id+"F0.wireOp",EDGE,"E23.trimOffspring")]}),-1.0]])],"derivedFrom":subQ0})])]}),makeQuery(id+"F29.opExtrude","SWEPT_FACE",FACE,{"disambiguationData":[OSD([sQuery(id+"F28.wireOp",EDGE,"E67.0")])]})]});}
            extrude(context, id + "F63", {"entities" : qUnion([Q0]), "operationType" : NewBodyOperationType.ADD, "endBound" : BoundingType.UP_TO_SURFACE, "oppositeDirection" : true, "depth" : 25 * mm, "endBoundEntityFace" : qUnion([Q1]), "offsetDistance" : 25 * mm, "hasSecondDirection" : true, "secondDirectionOppositeDirection" : false, "secondDirectionDepth" : 2 * mm});
        }
        {
            var Q0;
            Q0=makeQuery(id+"F45.imprint","IMPRINT",FACE,{"disambiguationData":[TD([[makeQuery(id+"F45.imprint","IMPRINT",EDGE,{"derivedFrom":sQuery(id+"F45.wireOp",EDGE,"E184")}),1.0]])]});
            var Q1;
            {var subQ0=sQuery(id+"F0.wireOp",EDGE,"E1");Q1=makeQuery(id+"F27.boolean.opBoolean","MERGE",FACE,{"derivedFrom":[makeQuery(id+"F1.opExtrude","SWEPT_FACE",FACE,{"disambiguationData":[OSD([subQ0]),TDD([makeQuery(id+"F0.imprint","IMPRINT",EDGE,{"disambiguationData":[TD([[makeQuery(id+"F0.imprint","INTERSECT",VERTEX,{"derivedFrom":[subQ0,sQuery(id+"F0.wireOp",EDGE,"E20.trimOffspring")]}),1.0]])],"derivedFrom":subQ0})])]}),makeQuery(id+"F27.opExtrude","SWEPT_FACE",FACE,{"disambiguationData":[OSD([sQuery(id+"F26.wireOp",EDGE,"E63.0")])]})]});}
            extrude(context, id + "F64", {"entities" : qUnion([Q0]), "operationType" : NewBodyOperationType.ADD, "endBound" : BoundingType.UP_TO_SURFACE, "oppositeDirection" : true, "depth" : 25 * mm, "endBoundEntityFace" : qUnion([Q1]), "offsetDistance" : 25 * mm});
        }
        {
            var Q0;
            Q0=makeQuery(id+"F45.imprint","IMPRINT",FACE,{"disambiguationData":[TD([[makeQuery(id+"F45.imprint","IMPRINT",EDGE,{"derivedFrom":sQuery(id+"F45.wireOp",EDGE,"E187")}),1.0]])]});
            var Q1;
            {var subQ0=sQuery(id+"F0.wireOp",EDGE,"E1");Q1=makeQuery(id+"F27.boolean.opBoolean","MERGE",FACE,{"derivedFrom":[makeQuery(id+"F1.opExtrude","SWEPT_FACE",FACE,{"disambiguationData":[OSD([subQ0]),TDD([makeQuery(id+"F0.imprint","IMPRINT",EDGE,{"disambiguationData":[TD([[makeQuery(id+"F0.imprint","INTERSECT",VERTEX,{"derivedFrom":[subQ0,sQuery(id+"F0.wireOp",EDGE,"E20.trimOffspring")]}),1.0]])],"derivedFrom":subQ0})])]}),makeQuery(id+"F27.opExtrude","SWEPT_FACE",FACE,{"disambiguationData":[OSD([sQuery(id+"F26.wireOp",EDGE,"E63.0")])]})]});}
            extrude(context, id + "F65", {"entities" : qUnion([Q0]), "operationType" : NewBodyOperationType.ADD, "endBound" : BoundingType.UP_TO_SURFACE, "oppositeDirection" : true, "depth" : 25 * mm, "endBoundEntityFace" : qUnion([Q1]), "offsetDistance" : 25 * mm, "hasSecondDirection" : true, "secondDirectionOppositeDirection" : false, "secondDirectionDepth" : 2 * mm});
        }
        {
            var Q0;
            Q0=makeQuery(id+"F54.opExtrude","CAP_EDGE",EDGE,{"disambiguationData":[OSD([sQuery(id+"F40.wireOp",EDGE,"E95")])],"isStart":true});
            var Q1;
            Q1=makeQuery(id+"F54.opExtrude","CAP_EDGE",EDGE,{"disambiguationData":[OSD([sQuery(id+"F40.wireOp",EDGE,"E96")])],"isStart":true});
            var Q2;
            Q2=makeQuery(id+"F56.opExtrude","CAP_EDGE",EDGE,{"disambiguationData":[OSD([sQuery(id+"F41.wireOp",EDGE,"E113")])],"isStart":true});
            var Q3;
            Q3=makeQuery(id+"F56.opExtrude","CAP_EDGE",EDGE,{"disambiguationData":[OSD([sQuery(id+"F41.wireOp",EDGE,"E114")])],"isStart":true});
            var Q4;
            Q4=makeQuery(id+"F58.opExtrude","CAP_EDGE",EDGE,{"disambiguationData":[OSD([sQuery(id+"F42.wireOp",EDGE,"E131")])],"isStart":true});
            var Q5;
            Q5=makeQuery(id+"F58.opExtrude","CAP_EDGE",EDGE,{"disambiguationData":[OSD([sQuery(id+"F42.wireOp",EDGE,"E132")])],"isStart":true});
            var Q6;
            Q6=makeQuery(id+"F60.opExtrude","CAP_EDGE",EDGE,{"disambiguationData":[OSD([sQuery(id+"F43.wireOp",EDGE,"E149")])],"isStart":true});
            var Q7;
            Q7=makeQuery(id+"F60.opExtrude","CAP_EDGE",EDGE,{"disambiguationData":[OSD([sQuery(id+"F43.wireOp",EDGE,"E150")])],"isStart":true});
            var Q8;
            Q8=makeQuery(id+"F62.opExtrude","CAP_EDGE",EDGE,{"disambiguationData":[OSD([sQuery(id+"F44.wireOp",EDGE,"E167")])],"isStart":true});
            var Q9;
            Q9=makeQuery(id+"F62.opExtrude","CAP_EDGE",EDGE,{"disambiguationData":[OSD([sQuery(id+"F44.wireOp",EDGE,"E168")])],"isStart":true});
            var Q10;
            Q10=makeQuery(id+"F64.opExtrude","CAP_EDGE",EDGE,{"disambiguationData":[OSD([sQuery(id+"F45.wireOp",EDGE,"E185")])],"isStart":true});
            var Q11;
            Q11=makeQuery(id+"F64.opExtrude","CAP_EDGE",EDGE,{"disambiguationData":[OSD([sQuery(id+"F45.wireOp",EDGE,"E186")])],"isStart":true});
            chamfer(context, id + "F66", {"entities" : qUnion([Q0, Q1, Q2, Q3, Q4, Q5, Q6, Q7, Q8, Q9, Q10, Q11]), "chamferType" : ChamferType.TWO_OFFSETS, "width1" : 0.25 * mm, "oppositeDirection" : false, "width2" : 0.3 * mm, "tangentPropagation" : true});
        }
        {
            var Q0;
            Q0=makeQuery(id+"F55.opExtrude","CAP_FACE",FACE,{"disambiguationData":[OSD([sQuery(id+"F40.wireOp",EDGE,"E97"),sQuery(id+"F40.wireOp",EDGE,"E98"),sQuery(id+"F40.wireOp",EDGE,"E99"),sQuery(id+"F40.wireOp",EDGE,"E100")])],"isStart":true});
            var Q1;
            Q1=makeQuery(id+"F61.opExtrude","CAP_FACE",FACE,{"disambiguationData":[OSD([sQuery(id+"F43.wireOp",EDGE,"E151"),sQuery(id+"F43.wireOp",EDGE,"E152"),sQuery(id+"F43.wireOp",EDGE,"E153"),sQuery(id+"F43.wireOp",EDGE,"E154")])],"isStart":true});
            var Q2;
            Q2=makeQuery(id+"F63.opExtrude","CAP_FACE",FACE,{"disambiguationData":[OSD([sQuery(id+"F44.wireOp",EDGE,"E169"),sQuery(id+"F44.wireOp",EDGE,"E170"),sQuery(id+"F44.wireOp",EDGE,"E171"),sQuery(id+"F44.wireOp",EDGE,"E172")])],"isStart":true});
            var Q3;
            Q3=makeQuery(id+"F65.opExtrude","CAP_FACE",FACE,{"disambiguationData":[OSD([sQuery(id+"F45.wireOp",EDGE,"E187"),sQuery(id+"F45.wireOp",EDGE,"E188"),sQuery(id+"F45.wireOp",EDGE,"E189"),sQuery(id+"F45.wireOp",EDGE,"E190")])],"isStart":true});
            var Q4;
            Q4=makeQuery(id+"F59.opExtrude","CAP_FACE",FACE,{"disambiguationData":[OSD([sQuery(id+"F42.wireOp",EDGE,"E133"),sQuery(id+"F42.wireOp",EDGE,"E134"),sQuery(id+"F42.wireOp",EDGE,"E135"),sQuery(id+"F42.wireOp",EDGE,"E136")])],"isStart":true});
            fillet(context, id + "F67", {"entities" : qUnion([Q0, Q1, Q2, Q3, Q4]), "radius" : 1.2 * mm, "tangentPropagation" : true, "allowEdgeOverflow" : false});
        }
        {
            var Q0;
            Q0=makeQuery(id+"F57.opExtrude","CAP_FACE",FACE,{"disambiguationData":[OSD([sQuery(id+"F41.wireOp",EDGE,"E115"),sQuery(id+"F41.wireOp",EDGE,"E116"),sQuery(id+"F41.wireOp",EDGE,"E117"),sQuery(id+"F41.wireOp",EDGE,"E118")])],"isStart":true});
            var sketch = newSketch(context, id + "F68", { "sketchPlane" : qUnion([Q0])});
            skLineSegment(sketch, "E201.0.0", {"start": v(-1.4, 16) * mm, "end": v(-1.4, 13) * mm});
            skLineSegment(sketch, "E201.0.1", {"start": v(-1.4, 13) * mm, "end": v(1.4, 13) * mm});
            skLineSegment(sketch, "E201.0.2", {"start": v(1.4, 13) * mm, "end": v(1.4, 16) * mm});
            skArc(sketch, "E201.0.3", {"start": v(1.4, 16) * mm, "mid": v(0, 17.4) * mm, "end": v(-1.4, 16) * mm});
            skLineSegment(sketch, "E202.0", {"start": v(-0.5, 16) * mm, "end": v(-0.5, 13.9) * mm});
            skArc(sketch, "E202.1", {"start": v(0.5, 16) * mm, "mid": v(0, 16.5) * mm, "end": v(-0.5, 16) * mm});
            skLineSegment(sketch, "E202.2", {"start": v(0.5, 13.9) * mm, "end": v(0.5, 16) * mm});
            skLineSegment(sketch, "E202.3", {"start": v(-0.5, 13.9) * mm, "end": v(0.5, 13.9) * mm});
            skSolve(sketch);
        }
        {
            var Q0;
            Q0=makeQuery(id+"F68.imprint","IMPRINT",FACE,{"disambiguationData":[TD([[makeQuery(id+"F68.imprint","IMPRINT",EDGE,{"derivedFrom":sQuery(id+"F68.wireOp",EDGE,"E202.0")}),1.0]])]});
            extrude(context, id + "F69", {"entities" : qUnion([Q0]), "operationType" : NewBodyOperationType.REMOVE, "oppositeDirection" : true, "depth" : 2 * mm, "offsetDistance" : 25 * mm});
        }
    });
